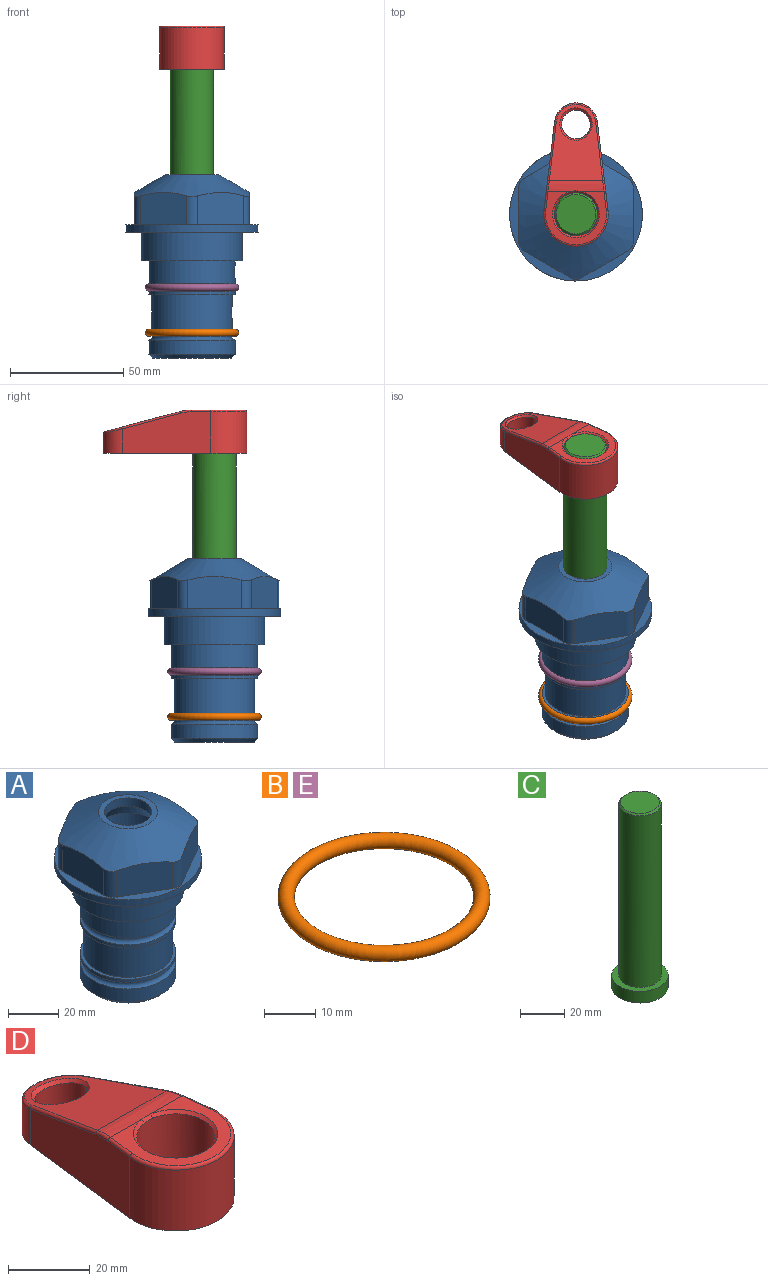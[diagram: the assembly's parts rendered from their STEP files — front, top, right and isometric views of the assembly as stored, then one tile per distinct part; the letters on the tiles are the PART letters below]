
ASSEMBLY  parts=5 mates=4
PART A: 36 faces, bbox 58.7x58.7x81 mm
  f0: cylinder r=17.78mm len=35.56mm, axis (0,0,1), area 1670.8mm2, adj f23,f24,f31
  f1: cylinder r=19.05mm len=38.1mm, axis (0,0,1), area 1191.9mm2, adj f26,f27,f30
  f2: plane 58.66x58.66mm, normal (0,0,-1), area 1150.6mm2, adj f3,f28
  f3: cylinder r=29.33mm len=58.66mm, axis (0,0,-1), area 585.1mm2, adj f2,f4
  f4: plane 58.66x58.66mm, normal (0,0,1), area 475.9mm2, adj f3,f5,f6,f7,f8,f9,f10,f11
  f5: plane 20.32x14.34mm, normal (-0.5,0.87,0), area 324.4mm2, adj f4,f15,f16,f17
  f6: plane 20.32x14.34mm, normal (0.5,0.87,0), area 324.4mm2, adj f4,f14,f15,f17
  f7: plane 23.48x14.34mm, normal (1,0,0), area 324.4mm2, adj f4,f13,f14,f17
  f8: plane 20.32x14.34mm, normal (0.5,-0.87,0), area 324.4mm2, adj f4,f12,f13,f17
  f9: plane 20.32x14.34mm, normal (-0.5,-0.87,0), area 324.4mm2, adj f4,f11,f12,f17
  f10: plane 23.48x14.34mm, normal (-1,0,0), area 324.4mm2, adj f4,f11,f16,f17
  f11: cylinder r=5.08mm len=12.85mm, axis (0,0,-1), area 67.2mm2, adj f4,f9,f10,f17
  f12: cylinder r=5.08mm len=12.85mm, axis (0,0,-1), area 67.2mm2, adj f4,f8,f9,f17
  f13: cylinder r=5.08mm len=12.85mm, axis (0,0,-1), area 67.2mm2, adj f4,f7,f8,f17
  f14: cylinder r=5.08mm len=12.85mm, axis (0,0,-1), area 67.2mm2, adj f4,f6,f7,f17
  f15: cylinder r=5.08mm len=12.85mm, axis (0,0,-1), area 67.2mm2, adj f4,f5,f6,f17
  f16: cylinder r=5.08mm len=12.85mm, axis (0,0,-1), area 67.2mm2, adj f4,f5,f10,f17
  f17: cone r=11.73mm half-angle=60deg, axis (0,0,-1), area 2071.8mm2, adj f5,f6,f7,f8,f9,f10,f11,f12
  f18: plane 23.46x23.46mm, normal (0,0,1), area 147.4mm2, adj f17,f35
  f19: plane 34.93x34.93mm, normal (0,0,-1), area 958mm2, adj f29
  f20: cylinder r=19.05mm len=38.1mm, axis (0,0,1), area 760.1mm2, adj f21,f29
  f21: torus R=19.05mm, axis (0,0,1), area 565.3mm2, adj f20,f22
  f22: cylinder r=19.05mm len=38.1mm, axis (0,0,1), area 190mm2, adj f21,f23
  f23: plane 38.1x38.1mm, normal (0,0,1), area 146.9mm2, adj f0,f22
  f24: plane 38.1x38.1mm, normal (0,0,-1), area 146.9mm2, adj f0,f25
  f25: cylinder r=19.05mm len=38.1mm, axis (0,0,1), area 190mm2, adj f24,f26
  f26: torus R=19.05mm, axis (0,0,1), area 565.3mm2, adj f1,f25
  f27: plane 44.45x44.45mm, normal (0,0,-1), area 411.7mm2, adj f1,f28
  f28: cylinder r=22.23mm len=44.45mm, axis (0,0,1), area 1773.5mm2, adj f2,f27
  f29: cone r=19.05mm half-angle=45deg, axis (0,0,1), area 257.5mm2, adj f19,f20
  f30: cylinder r=3.17mm len=6.75mm, axis (-1,0,0), area 128mm2, adj f1,f33
  f31: cylinder r=3.17mm len=6.35mm, axis (-1,0,0), area 102.5mm2, adj f0,f33
  f32: plane 25.4x25.4mm, normal (0,0,1), area 506.7mm2, adj f33
  f33: cylinder r=12.7mm len=66.42mm, axis (0,0,-1), area 5236.2mm2, adj f30,f31,f32,f34
  f34: cone r=9.53mm half-angle=30deg, axis (0,0,-1), area 443.4mm2, adj f33,f35
  f35: cylinder r=9.53mm len=19.05mm, axis (0,0,-1), area 240.9mm2, adj f18,f34
PART B: 1 faces, bbox 44.7x44.7x3.2 mm
  f0: torus R=19.05mm, axis (0,0,1), area 1193.9mm2
PART C: 6 faces, bbox 25.4x25.4x101.6 mm
  f0: plane 17.46x17.46mm, normal (0,0,1), area 239.5mm2, adj f5
  f1: plane 25.4x25.4mm, normal (0,0,-1), area 506.7mm2, adj f2
  f2: cylinder r=12.7mm len=25.4mm, axis (0,0,1), area 506.7mm2, adj f1,f3
  f3: plane 25.4x25.4mm, normal (0,0,1), area 221.7mm2, adj f2,f4
  f4: cylinder r=9.53mm len=94.46mm, axis (0,0,1), area 5653mm2, adj f3,f5
  f5: cone r=8.73mm half-angle=45deg, axis (0,0,-1), area 64.4mm2, adj f0,f4
PART D: 31 faces, bbox 31.7x65.5x19.8 mm
  f0: plane 39.12x18.26mm, normal (0.99,0.12,0), area 612.2mm2, adj f1,f4,f7,f11,f13,f15
  f1: cylinder r=9.53mm len=18.91mm, axis (0,0,-1), area 296.1mm2, adj f0,f2,f7,f17
  f2: plane 39.12x18.26mm, normal (-0.99,0.12,0), area 612.2mm2, adj f1,f4,f7,f12,f14,f16
  f3: cylinder r=6.35mm len=12.7mm, axis (0,0,-1), area 362.4mm2, adj f7,f18
  f4: cylinder r=14.29mm len=28.58mm, axis (0,0,-1), area 882.2mm2, adj f0,f2,f7,f10
  f5: cylinder r=9.53mm len=19.05mm, axis (0,0,-1), area 1092.6mm2, adj f7,f19,f20
  f6: plane 26.99x23.69mm, normal (0,0,1), area 216.2mm2, adj f9,f10,f11,f12,f19
  f7: plane 63.5x28.58mm, normal (0,0,-1), area 661.8mm2, adj f0,f1,f2,f3,f4,f5,f22,f23
  f8: plane 33.52x23.6mm, normal (0,0.26,0.97), area 486mm2, adj f9,f15,f16,f17,f18
  f9: cylinder r=19.05mm len=24.72mm, axis (1,0,0), area 120.4mm2, adj f6,f8,f13,f14,f20
  f10: torus R=13.49mm, axis (0,0,1), area 59mm2, adj f4,f6,f11,f12
  f11: cylinder r=0.79mm len=8.67mm, axis (0.12,-0.99,0), area 10.8mm2, adj f0,f6,f10,f13
  f12: cylinder r=0.79mm len=8.67mm, axis (0.12,0.99,0), area 10.8mm2, adj f2,f6,f10,f14
  f13: bspline ~4.95x1.42mm, area 6.1mm2, adj f0,f9,f11,f15
  f14: bspline ~4.95x1.42mm, area 6.1mm2, adj f2,f9,f12,f16
  f15: cylinder r=0.79mm len=25.95mm, axis (0.12,-0.96,0.26), area 32.9mm2, adj f0,f8,f13,f17
  f16: cylinder r=0.79mm len=25.95mm, axis (0.12,0.96,-0.26), area 32.9mm2, adj f2,f8,f14,f17
  f17: bspline ~18.91x8.38mm, area 30mm2, adj f1,f8,f15,f16
  f18: bspline ~14.29x14.29mm, area 48.3mm2, adj f3,f8
  f19: cone r=9.53mm half-angle=45deg, axis (0,0,1), area 66.5mm2, adj f5,f6,f20
  f20: bspline ~3.22x0.96mm, area 3.5mm2, adj f5,f9,f19
  f21: plane 2.75x2.72mm, normal (0,0,-1), area 2.9mm2, adj f23,f25,f28
  f22: plane 23.05x15.88mm, normal (-0.99,-0.12,0), area 323.6mm2, adj f7,f25,f26,f27,f28,f29
  f23: plane 23.05x15.88mm, normal (0.99,-0.12,0), area 323.6mm2, adj f7,f21,f25,f27,f28,f30
  f24: cylinder r=9.53mm len=10.69mm, axis (0,0,-1), area 114.7mm2, adj f7,f27,f29,f30
  f25: cylinder r=12.7mm len=20.59mm, axis (0,0,-1), area 381.1mm2, adj f7,f21,f22,f23,f26,f28
  f26: plane 2.75x2.72mm, normal (0,0,-1), area 2.9mm2, adj f22,f25,f28
  f27: plane 19.72x18.37mm, normal (0,-0.26,-0.97), area 291.8mm2, adj f22,f23,f24,f28,f29,f30
  f28: cylinder r=15.88mm len=19.92mm, axis (1,0,0), area 54.8mm2, adj f21,f22,f23,f25,f26,f27
  f29: cylinder r=1.59mm len=11mm, axis (0,0,-1), area 34.7mm2, adj f7,f22,f24,f27
  f30: cylinder r=1.59mm len=11mm, axis (0,0,-1), area 34.7mm2, adj f7,f23,f24,f27
PART E: same geometry as B
PLACE A t=(-15.38,-19.55,-2.09)mm
PLACE B t=(-15.38,-19.55,-22.1)mm
PLACE C t=(-15.38,-19.55,25.46)mm
PLACE D t=(-15.38,-19.55,25.46)mm
PLACE E t=(-15.38,-19.55,-2.09)mm
MATE fastened D.f4 <-> C.f2  axis (0,0,1) through (-15.38,-19.55,88.96)mm
MATE fastened B.f0 <-> A.f0  axis (0,0,1) through (-15.38,-19.55,-46.61)mm
MATE fastened E.f0 <-> A.f0  axis (0,0,1) through (-15.38,-19.55,-26.61)mm
MATE cylindrical C.f2 <-> A.f0  axis (0,0,-1) through (-15.38,-19.55,-12.64)mm
